# Revit family: РИДАН_ Реле перепада давления воздуха DP100
name_source: partatom
category: Арматура воздуховодов
units: mm (PartAtom-declared; Revit-internal decimal feet)

## family parameters
Всегда вертикально = Да
На основе рабочей плоскости = Нет
Общий = Нет
При загрузке вырезать с полостями = Нет
Размер круглого соединителя = Использовать диаметр
Тип детали = Присоединяется

## types (8) — shared parameters
ADSK_Версия Revit = 2019
ADSK_Версия семейства = 1.0
ADSK_Единица измерения = шт.
ADSK_Завод-изготовитель = ООО «Ридан-Трейд»
ADSK_Количество = 1
ADSK_Марка = DP100
ADSK_Масса = 0.5
LT = DP100

## per-type parameters (varying)
| type | A | ADSK_Код изделия | ADSK_Наименование |
| 017D000200R, 20_200 Па, 10 Па | 1 мм | 017D000200R | Реле перепада давления воздуха DP100, Диапазон уставок 20...200 Па, Настаиваемый дифференциал 10 Па |
| 017D000300R, 30_300 Па, 10 Па | 2 мм | 017D000300R | Реле перепада давления воздуха DP100, Диапазон уставок 30...300 Па, Настаиваемый дифференциал 10 Па |
| 017D000400R, 40_400 Па, 20 Па | 3 мм | 017D000400R | Реле перепада давления воздуха DP100, Диапазон уставок 40...400 Па, Настаиваемый дифференциал 20 Па |
| 017D000500R, 50_500 Па, 20 Па | 4 мм | 017D000500R | Реле перепада давления воздуха DP100, Диапазон уставок 50...500 Па, Настаиваемый дифференциал 20 Па |
| 017D001000R, 200_1000 Па, 100 Па | 5 мм | 017D001000R | Реле перепада давления воздуха DP100, Диапазон уставок 200...1000 Па, Настаиваемый дифференциал 100 Па |
| 017D001001R, 100_1000 Па, 50 Па | 6 мм | 017D001001R | Реле перепада давления воздуха DP100, Диапазон уставок 100...1000 Па, Настаиваемый дифференциал 50 Па |
| 017D002500R, 500_2500 Па, 150 Па | 7 мм | 017D002500R | Реле перепада давления воздуха DP100, Диапазон уставок 500...2500 Па, Настаиваемый дифференциал 150 Па |
| 017D005000R, 1000_5000 Па, 250 Па | 8 мм | 017D005000R | Реле перепада давления воздуха DP100, Диапазон уставок 1000...5000 Па, Настаиваемый дифференциал 250 Па |
